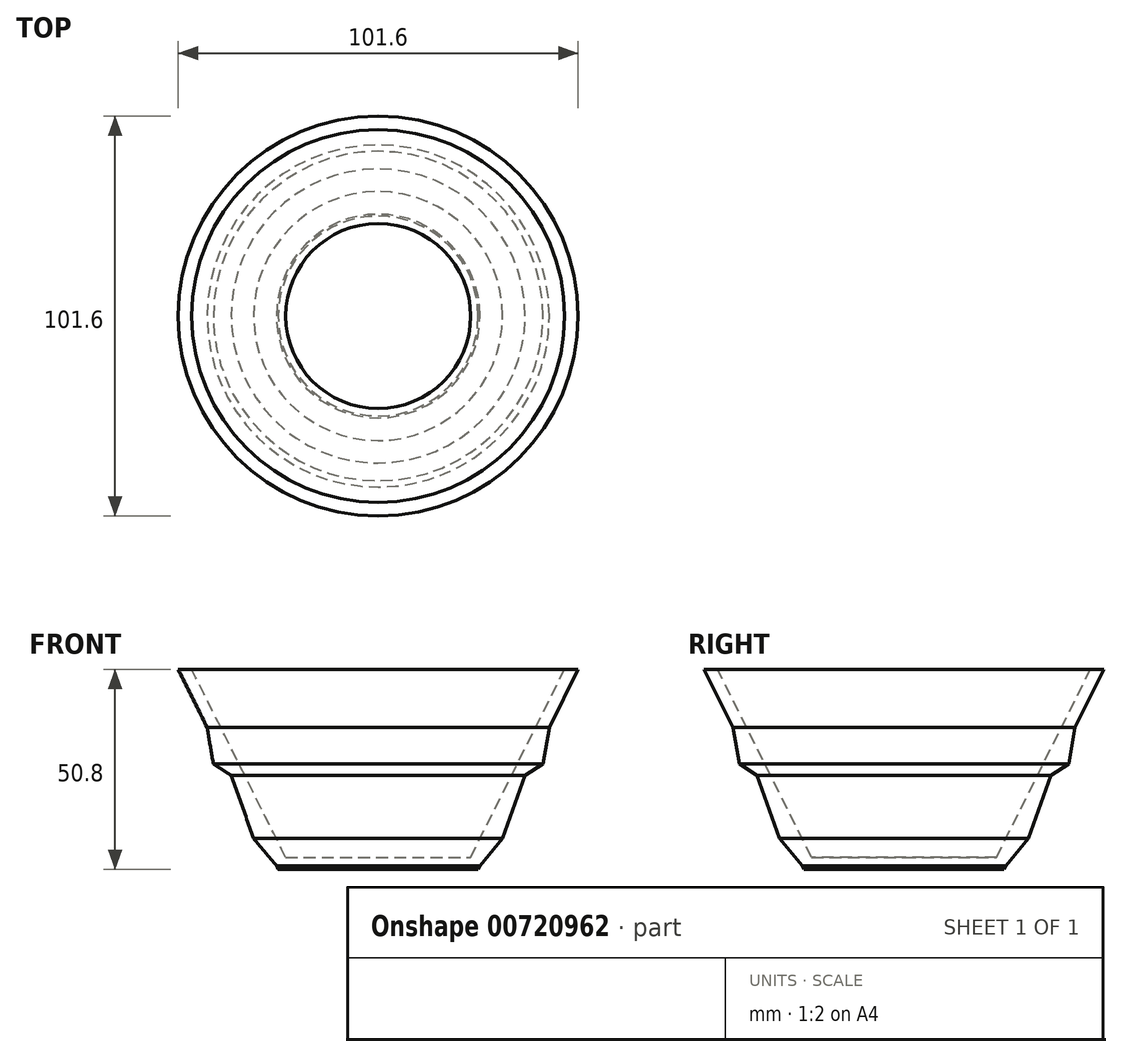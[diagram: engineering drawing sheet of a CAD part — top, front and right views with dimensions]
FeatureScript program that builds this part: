
annotation { "Feature Type Name" : "Feature", "Feature Type Description" : "" }
export const myFeature = defineFeature(function(context is Context, id is Id, definition is map)
    precondition{}
    {
        {
            var Q0;
            Q0=qCreatedBy(makeId("Front.planeOp"),FACE);
            var sketch = newSketch(context, id + "F0", { "sketchPlane" : qUnion([Q0])});
            skLineSegment(sketch, "E0", {"start": v(0, 0) * mm, "end": v(0, 50.8) * mm, "construction": true});
            skLineSegment(sketch, "E1", {"start": v(0, 0) * mm, "end": v(25.4, 0) * mm});
            skLineSegment(sketch, "E2", {"start": v(25.4, 0) * mm, "end": v(50.8, 50.8) * mm});
            skLineSegment(sketch, "E3.0", {"start": v(23.5, 3.07) * mm, "end": v(47.36, 50.8) * mm});
            skLineSegment(sketch, "E3.1", {"start": v(0, 3.07) * mm, "end": v(23.5, 3.07) * mm});
            skLineSegment(sketch, "E4", {"start": v(0, 3.07) * mm, "end": v(0, 0) * mm});
            skLineSegment(sketch, "E5", {"start": v(47.36, 50.8) * mm, "end": v(50.8, 50.8) * mm});
            skLineSegment(sketch, "E6", {"start": v(43.46, 36.13) * mm, "end": v(41.86, 26.75) * mm});
            skLineSegment(sketch, "E7", {"start": v(41.86, 26.75) * mm, "end": v(37.34, 23.89) * mm});
            skLineSegment(sketch, "E8", {"start": v(37.34, 23.89) * mm, "end": v(31.63, 7.84) * mm});
            skLineSegment(sketch, "E9", {"start": v(31.63, 7.84) * mm, "end": v(25.86, 0.92) * mm});
            skSolve(sketch);
        }
        {
            var Q0;
            Q0=makeQuery(id+"F0.imprint","IMPRINT",FACE,{"disambiguationData":[TD([[makeQuery(id+"F0.imprint","IMPRINT",EDGE,{"derivedFrom":sQuery(id+"F0.wireOp",EDGE,"E1")}),1.0]])]});
            var Q1;
            {var subQ0=sQuery(id+"F0.wireOp",EDGE,"E6");Q1=makeQuery(id+"F0.imprint","IMPRINT",FACE,{"disambiguationData":[TD([[makeQuery(id+"F0.imprint","IMPRINT",EDGE,{"derivedFrom":subQ0}),-1.0]])]});}
            var Q2;
            {var subQ0=sQuery(id+"F0.wireOp",EDGE,"E8");Q2=makeQuery(id+"F0.imprint","IMPRINT",FACE,{"disambiguationData":[TD([[makeQuery(id+"F0.imprint","IMPRINT",EDGE,{"derivedFrom":subQ0}),-1.0]])]});}
            var Q3;
            Q3=sQuery(id+"F0.wireOp",EDGE,"E0");
            revolve(context, id + "F1", {"surfaceOperationType" : NewSurfaceOperationType.NEW, "entities" : qUnion([Q0, Q1, Q2]), "axis" : qUnion([Q3]), "revolveType" : RevolveType.FULL});
        }
    });
